SOLIDWORKS PART (.sldprt)
format: sldprt  version: not decoded by parser v0  size: 407,552 bytes
history: native  units: mm
features: sketch x7, plane x6, mirror x2, cut_extrude x2, extrude x2, material x1, sweep x1 (+10 scaffold rows collapsed)
feature tree (31):
  scaffold x10  (default folders/planes/origin — collapsed)
  material  "Matériau <non spécifié>"
  plane  "Plan de face"
  plane  "Plan de dessus"
  plane  "Plan de droite"
  sketch  "Esquisse3"  dims[c1.D6=50.0mm c1.D7=10.0mm c2.D6=34.0mm c2.D1=60.0mm c2.D2=103.0mm c2.D3=100.0mm c2.D4=63.0mm c2.D5=115.0mm c3.D1=37.0mm c3.D3=122.0mm c3.D4=68.0mm c3.D5=43.5mm c3.D2=67.0mm c3.D7=55.5mm c3.D8=~35.356611mm c4.D2=71.0mm c4.D5=49.5mm c4.D6=~34.004632mm c4.D8=8.0mm c4.D7=16.0mm]
  sketch  "Esquisse1"  dims[c1.D1=16.0mm c1.D2=16.0mm c2.D1=16.0mm c2.D2=2.5mm]
  sweep  "Balayage2"
  mirror  "Symétrie1"
  plane  "Plan1"  Offset=8mm
  plane  "Plan2"
  sketch  "Esquisse4"
  cut_extrude  "Enlèv. mat.-Extru.1"  [1 undecoded]
  sketch  "Esquisse5"  dims[c1.D2=14.0mm c1.D4=3.5mm c1.D1=30.5mm c1.D3=7.0mm c2.D4=14.0mm c2.D5=9.0mm]
  extrude  "Extrusion1"  Depth=4.5mm
  plane  "Plan3"  Offset=63mm
  sketch  "Esquisse6"  dims[c1.D1=12.0mm c1.D2=12.0mm c1.D3=4.2mm c2.D2=81.0mm]
  extrude  "Extrusion2"  [1 undecoded]
  mirror  "Symétrie2"
  sketch  "Esquisse7"  dims[D1=5.5mm]
  cut_extrude  "Enlèv. mat.-Extru.2"  [1 undecoded]
  sketch  "Esquisse8"
decode coverage: 6 of 14 modeling features carry decoded parameters
note: ~ marks probable driven/reference dimensions
note: 3 parameter values undecoded
summary: no parameter record found for 3 features
note: suppression state not decoded; provenance and decode notes live in map.json
